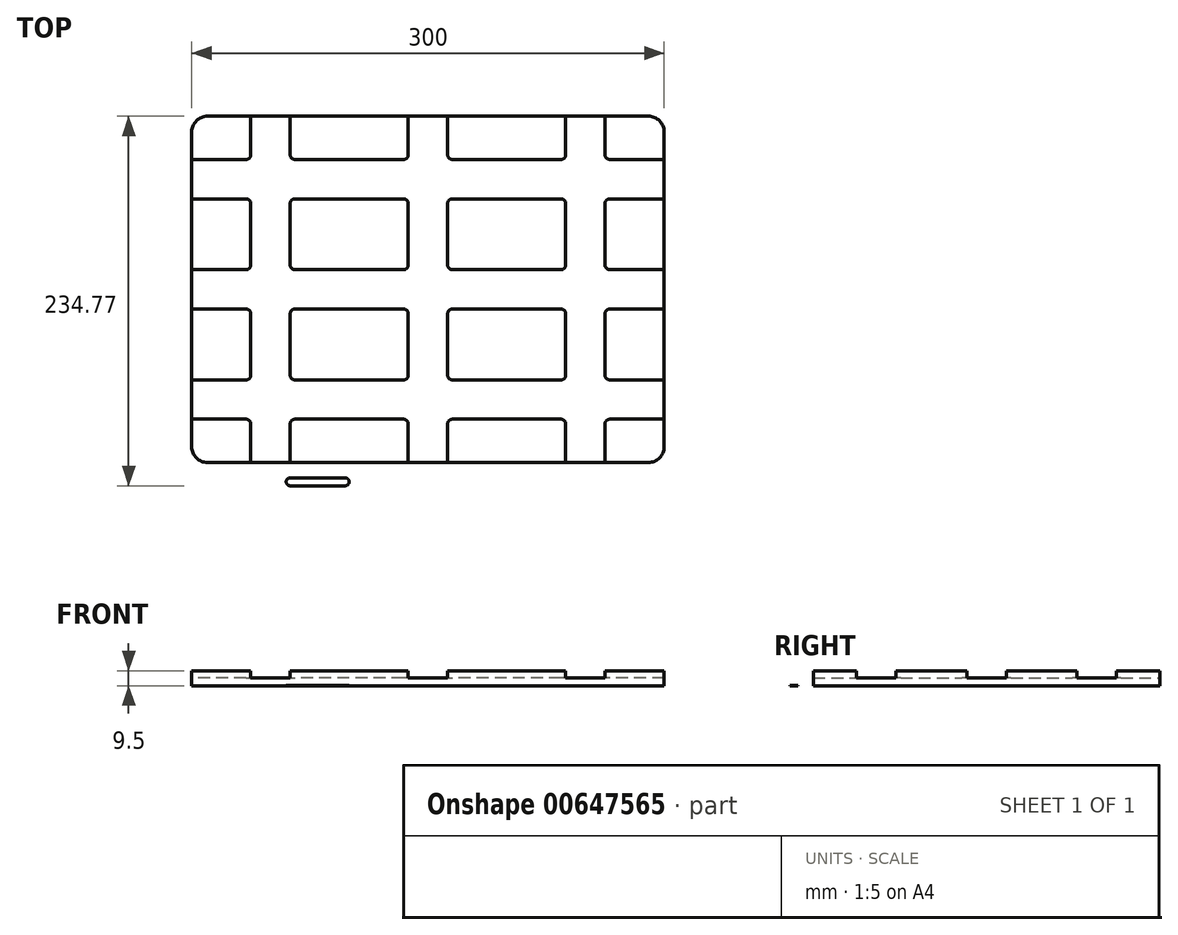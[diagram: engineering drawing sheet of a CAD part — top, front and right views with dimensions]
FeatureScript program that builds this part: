
annotation { "Feature Type Name" : "Feature", "Feature Type Description" : "" }
export const myFeature = defineFeature(function(context is Context, id is Id, definition is map)
    precondition{}
    {
        {
            var Q0;
            Q0=qCreatedBy(makeId("Top.planeOp"),FACE);
            var sketch = newSketch(context, id + "F0", { "sketchPlane" : qUnion([Q0])});
            skLineSegment(sketch, "E0.bottom", {"start": v(140, -110) * mm, "end": v(-140, -110) * mm});
            skLineSegment(sketch, "E0.top", {"start": v(140, 110) * mm, "end": v(-140, 110) * mm});
            skLineSegment(sketch, "E0.left", {"start": v(150, -100) * mm, "end": v(150, 100) * mm});
            skLineSegment(sketch, "E0.right", {"start": v(-150, -100) * mm, "end": v(-150, 100) * mm});
            skPoint(sketch, "E0.middle", {"position": v(0, 0) * mm});
            skLineSegment(sketch, "E1", {"start": v(0, 110) * mm, "end": v(0, -110) * mm, "construction": true});
            skLineSegment(sketch, "E2", {"start": v(-12.5, 124.5) * mm, "end": v(12.5, 124.5) * mm});
            skPoint(sketch, "E3", {"position": v(0, 124.5) * mm});
            skLineSegment(sketch, "E4", {"start": v(-12.5, 110) * mm, "end": v(-12.5, 85.5) * mm});
            skLineSegment(sketch, "E5", {"start": v(12.5, 110) * mm, "end": v(12.5, 85.5) * mm});
            skLineSegment(sketch, "E6", {"start": v(-168.64, 12.5) * mm, "end": v(-168.64, -12.5) * mm});
            skPoint(sketch, "E7", {"position": v(-168.64, 0) * mm});
            skLineSegment(sketch, "E8", {"start": v(-150, 12.5) * mm, "end": v(-115.5, 12.5) * mm});
            skLineSegment(sketch, "E9", {"start": v(-150, -12.5) * mm, "end": v(-115.5, -12.5) * mm});
            skLineSegment(sketch, "E10", {"start": v(-100, 110) * mm, "end": v(-100, -110) * mm, "construction": true});
            skLineSegment(sketch, "E11", {"start": v(100, -110) * mm, "end": v(100, 110) * mm, "construction": true});
            skLineSegment(sketch, "E12", {"start": v(-112.5, 122.6) * mm, "end": v(-87.5, 122.6) * mm});
            skPoint(sketch, "E13", {"position": v(-100, 122.6) * mm});
            skLineSegment(sketch, "E14", {"start": v(87.5, 126.02) * mm, "end": v(112.5, 126.02) * mm});
            skPoint(sketch, "E15", {"position": v(100, 126.02) * mm});
            skLineSegment(sketch, "E16", {"start": v(-112.5, 110) * mm, "end": v(-112.5, 85.5) * mm});
            skLineSegment(sketch, "E17", {"start": v(-87.5, 110) * mm, "end": v(-87.5, 85.5) * mm});
            skLineSegment(sketch, "E18", {"start": v(87.5, 110) * mm, "end": v(87.5, 85.5) * mm});
            skLineSegment(sketch, "E19", {"start": v(112.5, 110) * mm, "end": v(112.5, 85.5) * mm});
            skLineSegment(sketch, "E20", {"start": v(-150, 70) * mm, "end": v(150, 70) * mm, "construction": true});
            skLineSegment(sketch, "E21", {"start": v(150, -70) * mm, "end": v(-150, -70) * mm, "construction": true});
            skLineSegment(sketch, "E22", {"start": v(-168.26, 82.5) * mm, "end": v(-168.26, 57.5) * mm});
            skLineSegment(sketch, "E23", {"start": v(-167.5, -57.5) * mm, "end": v(-167.5, -82.5) * mm});
            skPoint(sketch, "E24", {"position": v(-168.26, 70) * mm});
            skPoint(sketch, "E25", {"position": v(-167.5, -70) * mm});
            skLineSegment(sketch, "E26", {"start": v(-150, 82.5) * mm, "end": v(-115.5, 82.5) * mm});
            skLineSegment(sketch, "E27", {"start": v(-150, 57.5) * mm, "end": v(-115.5, 57.5) * mm});
            skLineSegment(sketch, "E28", {"start": v(-150, -57.5) * mm, "end": v(-115.5, -57.5) * mm});
            skLineSegment(sketch, "E29", {"start": v(-150, -82.5) * mm, "end": v(-115.5, -82.5) * mm});
            skLineSegment(sketch, "E30.trimOffspring", {"start": v(-84.5, 82.5) * mm, "end": v(-15.5, 82.5) * mm});
            skLineSegment(sketch, "E31.trimOffspring", {"start": v(-112.5, 54.5) * mm, "end": v(-112.5, 15.5) * mm});
            skLineSegment(sketch, "E32.trimOffspring", {"start": v(-84.5, 57.5) * mm, "end": v(-15.5, 57.5) * mm});
            skLineSegment(sketch, "E33.trimOffspring", {"start": v(-87.5, 54.5) * mm, "end": v(-87.5, 15.5) * mm});
            skLineSegment(sketch, "E34.trimOffspring", {"start": v(-12.5, 54.5) * mm, "end": v(-12.5, 15.5) * mm});
            skLineSegment(sketch, "E35.trimOffspring", {"start": v(15.5, 82.5) * mm, "end": v(84.5, 82.5) * mm});
            skLineSegment(sketch, "E36.trimOffspring", {"start": v(12.5, 54.5) * mm, "end": v(12.5, 15.5) * mm});
            skLineSegment(sketch, "E37.trimOffspring", {"start": v(15.5, 57.5) * mm, "end": v(84.5, 57.5) * mm});
            skLineSegment(sketch, "E38.trimOffspring", {"start": v(87.5, 54.5) * mm, "end": v(87.5, 15.5) * mm});
            skLineSegment(sketch, "E39.trimOffspring", {"start": v(115.5, 57.5) * mm, "end": v(150, 57.5) * mm});
            skLineSegment(sketch, "E40.trimOffspring", {"start": v(112.5, 54.5) * mm, "end": v(112.5, 15.5) * mm});
            skLineSegment(sketch, "E41.trimOffspring", {"start": v(-84.5, 12.5) * mm, "end": v(-15.5, 12.5) * mm});
            skLineSegment(sketch, "E42.trimOffspring", {"start": v(-84.5, -12.5) * mm, "end": v(-15.5, -12.5) * mm});
            skLineSegment(sketch, "E43.trimOffspring", {"start": v(-112.5, -15.5) * mm, "end": v(-112.5, -54.5) * mm});
            skLineSegment(sketch, "E44.trimOffspring", {"start": v(-87.5, -15.5) * mm, "end": v(-87.5, -54.5) * mm});
            skLineSegment(sketch, "E45.trimOffspring", {"start": v(-12.5, -15.5) * mm, "end": v(-12.5, -54.5) * mm});
            skLineSegment(sketch, "E46.trimOffspring", {"start": v(12.5, -15.5) * mm, "end": v(12.5, -54.5) * mm});
            skLineSegment(sketch, "E47.trimOffspring", {"start": v(87.5, -15.5) * mm, "end": v(87.5, -54.5) * mm});
            skLineSegment(sketch, "E48.trimOffspring", {"start": v(112.5, -15.5) * mm, "end": v(112.5, -54.5) * mm});
            skLineSegment(sketch, "E49.trimOffspring", {"start": v(115.5, 12.5) * mm, "end": v(150, 12.5) * mm});
            skLineSegment(sketch, "E50.trimOffspring", {"start": v(115.5, -12.5) * mm, "end": v(150, -12.5) * mm});
            skLineSegment(sketch, "E51.trimOffspring", {"start": v(-112.5, -85.5) * mm, "end": v(-112.5, -110) * mm});
            skLineSegment(sketch, "E52.trimOffspring", {"start": v(-84.5, -82.5) * mm, "end": v(-15.5, -82.5) * mm});
            skLineSegment(sketch, "E53.trimOffspring", {"start": v(-87.5, -85.5) * mm, "end": v(-87.5, -110) * mm});
            skLineSegment(sketch, "E54.trimOffspring", {"start": v(-84.5, -57.5) * mm, "end": v(-15.5, -57.5) * mm});
            skLineSegment(sketch, "E55.trimOffspring", {"start": v(15.5, -57.5) * mm, "end": v(84.5, -57.5) * mm});
            skLineSegment(sketch, "E56.trimOffspring", {"start": v(-12.5, -85.5) * mm, "end": v(-12.5, -110) * mm});
            skLineSegment(sketch, "E57.trimOffspring", {"start": v(15.5, -82.5) * mm, "end": v(84.5, -82.5) * mm});
            skLineSegment(sketch, "E58.trimOffspring", {"start": v(12.5, -85.5) * mm, "end": v(12.5, -110) * mm});
            skLineSegment(sketch, "E59.trimOffspring", {"start": v(87.5, -85.5) * mm, "end": v(87.5, -110) * mm});
            skLineSegment(sketch, "E60.trimOffspring", {"start": v(115.5, -82.5) * mm, "end": v(150, -82.5) * mm});
            skLineSegment(sketch, "E61.trimOffspring", {"start": v(112.5, -85.5) * mm, "end": v(112.5, -110) * mm});
            skLineSegment(sketch, "E62.trimOffspring", {"start": v(115.5, -57.5) * mm, "end": v(150, -57.5) * mm});
            skLineSegment(sketch, "E63.trimOffspring", {"start": v(115.5, 82.5) * mm, "end": v(150, 82.5) * mm});
            skPoint(sketch, "E64.visualSharp", {"position": v(-150, 110) * mm});
            skArc(sketch, "E64.filletArc", {"start": v(-140, 110) * mm, "mid": v(-147.07, 107.07) * mm, "end": v(-150, 100) * mm});
            skPoint(sketch, "E65.visualSharp", {"position": v(-150, -110) * mm});
            skArc(sketch, "E65.filletArc", {"start": v(-150, -100) * mm, "mid": v(-147.07, -107.07) * mm, "end": v(-140, -110) * mm});
            skPoint(sketch, "E66.visualSharp", {"position": v(150, -110) * mm});
            skArc(sketch, "E66.filletArc", {"start": v(140, -110) * mm, "mid": v(147.07, -107.07) * mm, "end": v(150, -100) * mm});
            skPoint(sketch, "E67.visualSharp", {"position": v(150, 110) * mm});
            skArc(sketch, "E67.filletArc", {"start": v(150, 100) * mm, "mid": v(147.07, 107.07) * mm, "end": v(140, 110) * mm});
            skPoint(sketch, "E68.visualSharp", {"position": v(112.5, -82.5) * mm});
            skArc(sketch, "E68.filletArc", {"start": v(115.5, -82.5) * mm, "mid": v(113.38, -83.38) * mm, "end": v(112.5, -85.5) * mm});
            skPoint(sketch, "E69.visualSharp", {"position": v(87.5, -82.5) * mm});
            skArc(sketch, "E69.filletArc", {"start": v(87.5, -85.5) * mm, "mid": v(86.62, -83.38) * mm, "end": v(84.5, -82.5) * mm});
            skPoint(sketch, "E70.visualSharp", {"position": v(112.5, -57.5) * mm});
            skArc(sketch, "E70.filletArc", {"start": v(112.5, -54.5) * mm, "mid": v(113.38, -56.62) * mm, "end": v(115.5, -57.5) * mm});
            skPoint(sketch, "E71.visualSharp", {"position": v(87.5, -57.5) * mm});
            skArc(sketch, "E71.filletArc", {"start": v(84.5, -57.5) * mm, "mid": v(86.62, -56.62) * mm, "end": v(87.5, -54.5) * mm});
            skPoint(sketch, "E72.visualSharp", {"position": v(12.5, -82.5) * mm});
            skArc(sketch, "E72.filletArc", {"start": v(15.5, -82.5) * mm, "mid": v(13.38, -83.38) * mm, "end": v(12.5, -85.5) * mm});
            skPoint(sketch, "E73.visualSharp", {"position": v(-12.5, -82.5) * mm});
            skArc(sketch, "E73.filletArc", {"start": v(-12.5, -85.5) * mm, "mid": v(-13.38, -83.38) * mm, "end": v(-15.5, -82.5) * mm});
            skPoint(sketch, "E74.visualSharp", {"position": v(-12.5, -57.5) * mm});
            skArc(sketch, "E74.filletArc", {"start": v(-15.5, -57.5) * mm, "mid": v(-13.38, -56.62) * mm, "end": v(-12.5, -54.5) * mm});
            skLineSegment(sketch, "E75.trimOffspring", {"start": v(15.5, 12.5) * mm, "end": v(84.5, 12.5) * mm});
            skPoint(sketch, "E76.visualSharp", {"position": v(12.5, -57.5) * mm});
            skArc(sketch, "E76.filletArc", {"start": v(12.5, -54.5) * mm, "mid": v(13.38, -56.62) * mm, "end": v(15.5, -57.5) * mm});
            skPoint(sketch, "E77.visualSharp", {"position": v(12.5, 12.5) * mm});
            skArc(sketch, "E77.filletArc", {"start": v(12.5, 15.5) * mm, "mid": v(13.38, 13.38) * mm, "end": v(15.5, 12.5) * mm});
            skPoint(sketch, "E78.visualSharp", {"position": v(87.5, 12.5) * mm});
            skArc(sketch, "E78.filletArc", {"start": v(84.5, 12.5) * mm, "mid": v(86.62, 13.38) * mm, "end": v(87.5, 15.5) * mm});
            skPoint(sketch, "E79.visualSharp", {"position": v(112.5, 12.5) * mm});
            skArc(sketch, "E79.filletArc", {"start": v(112.5, 15.5) * mm, "mid": v(113.38, 13.38) * mm, "end": v(115.5, 12.5) * mm});
            skPoint(sketch, "E80.visualSharp", {"position": v(87.5, -12.5) * mm});
            skArc(sketch, "E80.filletArc", {"start": v(87.5, -15.5) * mm, "mid": v(86.62, -13.38) * mm, "end": v(84.5, -12.5) * mm});
            skPoint(sketch, "E81.visualSharp", {"position": v(112.5, -12.5) * mm});
            skArc(sketch, "E81.filletArc", {"start": v(115.5, -12.5) * mm, "mid": v(113.38, -13.38) * mm, "end": v(112.5, -15.5) * mm});
            skPoint(sketch, "E82.visualSharp", {"position": v(-87.5, -57.5) * mm});
            skArc(sketch, "E82.filletArc", {"start": v(-87.5, -54.5) * mm, "mid": v(-86.62, -56.62) * mm, "end": v(-84.5, -57.5) * mm});
            skPoint(sketch, "E83.visualSharp", {"position": v(-87.5, -12.5) * mm});
            skArc(sketch, "E83.filletArc", {"start": v(-84.5, -12.5) * mm, "mid": v(-86.62, -13.38) * mm, "end": v(-87.5, -15.5) * mm});
            skPoint(sketch, "E84.visualSharp", {"position": v(-87.5, 12.5) * mm});
            skArc(sketch, "E84.filletArc", {"start": v(-87.5, 15.5) * mm, "mid": v(-86.62, 13.38) * mm, "end": v(-84.5, 12.5) * mm});
            skPoint(sketch, "E85.visualSharp", {"position": v(-12.5, 12.5) * mm});
            skArc(sketch, "E85.filletArc", {"start": v(-15.5, 12.5) * mm, "mid": v(-13.38, 13.38) * mm, "end": v(-12.5, 15.5) * mm});
            skPoint(sketch, "E86.visualSharp", {"position": v(-12.5, 57.5) * mm});
            skArc(sketch, "E86.filletArc", {"start": v(-12.5, 54.5) * mm, "mid": v(-13.38, 56.62) * mm, "end": v(-15.5, 57.5) * mm});
            skPoint(sketch, "E87.visualSharp", {"position": v(12.5, 57.5) * mm});
            skArc(sketch, "E87.filletArc", {"start": v(15.5, 57.5) * mm, "mid": v(13.38, 56.62) * mm, "end": v(12.5, 54.5) * mm});
            skPoint(sketch, "E88.visualSharp", {"position": v(112.5, 82.5) * mm});
            skArc(sketch, "E88.filletArc", {"start": v(112.5, 85.5) * mm, "mid": v(113.38, 83.38) * mm, "end": v(115.5, 82.5) * mm});
            skPoint(sketch, "E89.visualSharp", {"position": v(87.5, 82.5) * mm});
            skArc(sketch, "E89.filletArc", {"start": v(84.5, 82.5) * mm, "mid": v(86.62, 83.38) * mm, "end": v(87.5, 85.5) * mm});
            skPoint(sketch, "E90.visualSharp", {"position": v(12.5, 82.5) * mm});
            skArc(sketch, "E90.filletArc", {"start": v(12.5, 85.5) * mm, "mid": v(13.38, 83.38) * mm, "end": v(15.5, 82.5) * mm});
            skPoint(sketch, "E91.visualSharp", {"position": v(-12.5, 82.5) * mm});
            skArc(sketch, "E91.filletArc", {"start": v(-15.5, 82.5) * mm, "mid": v(-13.38, 83.38) * mm, "end": v(-12.5, 85.5) * mm});
            skPoint(sketch, "E92.visualSharp", {"position": v(-87.5, 82.5) * mm});
            skArc(sketch, "E92.filletArc", {"start": v(-87.5, 85.5) * mm, "mid": v(-86.62, 83.38) * mm, "end": v(-84.5, 82.5) * mm});
            skPoint(sketch, "E93.visualSharp", {"position": v(-112.5, 82.5) * mm});
            skArc(sketch, "E93.filletArc", {"start": v(-115.5, 82.5) * mm, "mid": v(-113.38, 83.38) * mm, "end": v(-112.5, 85.5) * mm});
            skPoint(sketch, "E94.visualSharp", {"position": v(-112.5, 57.5) * mm});
            skArc(sketch, "E94.filletArc", {"start": v(-112.5, 54.5) * mm, "mid": v(-113.38, 56.62) * mm, "end": v(-115.5, 57.5) * mm});
            skPoint(sketch, "E95.visualSharp", {"position": v(-87.5, 57.5) * mm});
            skArc(sketch, "E95.filletArc", {"start": v(-84.5, 57.5) * mm, "mid": v(-86.62, 56.62) * mm, "end": v(-87.5, 54.5) * mm});
            skPoint(sketch, "E96.visualSharp", {"position": v(-112.5, 12.5) * mm});
            skArc(sketch, "E96.filletArc", {"start": v(-115.5, 12.5) * mm, "mid": v(-113.38, 13.38) * mm, "end": v(-112.5, 15.5) * mm});
            skPoint(sketch, "E97.visualSharp", {"position": v(-112.5, -12.5) * mm});
            skArc(sketch, "E97.filletArc", {"start": v(-112.5, -15.5) * mm, "mid": v(-113.38, -13.38) * mm, "end": v(-115.5, -12.5) * mm});
            skPoint(sketch, "E98.visualSharp", {"position": v(-112.5, -57.5) * mm});
            skArc(sketch, "E98.filletArc", {"start": v(-115.5, -57.5) * mm, "mid": v(-113.38, -56.62) * mm, "end": v(-112.5, -54.5) * mm});
            skPoint(sketch, "E99.visualSharp", {"position": v(-112.5, -82.5) * mm});
            skArc(sketch, "E99.filletArc", {"start": v(-112.5, -85.5) * mm, "mid": v(-113.38, -83.38) * mm, "end": v(-115.5, -82.5) * mm});
            skPoint(sketch, "E100.visualSharp", {"position": v(-87.5, -82.5) * mm});
            skArc(sketch, "E100.filletArc", {"start": v(-84.5, -82.5) * mm, "mid": v(-86.62, -83.38) * mm, "end": v(-87.5, -85.5) * mm});
            skPoint(sketch, "E101.visualSharp", {"position": v(112.5, 57.5) * mm});
            skArc(sketch, "E101.filletArc", {"start": v(115.5, 57.5) * mm, "mid": v(113.38, 56.62) * mm, "end": v(112.5, 54.5) * mm});
            skPoint(sketch, "E102.visualSharp", {"position": v(87.5, 57.5) * mm});
            skArc(sketch, "E102.filletArc", {"start": v(87.5, 54.5) * mm, "mid": v(86.62, 56.62) * mm, "end": v(84.5, 57.5) * mm});
            skLineSegment(sketch, "E103.trimOffspring", {"start": v(15.5, -12.5) * mm, "end": v(84.5, -12.5) * mm});
            skPoint(sketch, "E104.visualSharp", {"position": v(12.5, -12.5) * mm});
            skArc(sketch, "E104.filletArc", {"start": v(15.5, -12.5) * mm, "mid": v(13.38, -13.38) * mm, "end": v(12.5, -15.5) * mm});
            skPoint(sketch, "E105.visualSharp", {"position": v(-12.5, -12.5) * mm});
            skArc(sketch, "E105.filletArc", {"start": v(-12.5, -15.5) * mm, "mid": v(-13.38, -13.38) * mm, "end": v(-15.5, -12.5) * mm});
            skLineSegment(sketch, "E106.bottom", {"start": v(-87.5, -119.77) * mm, "end": v(-52.5, -119.77) * mm});
            skLineSegment(sketch, "E106.top", {"start": v(-87.5, -124.77) * mm, "end": v(-52.5, -124.77) * mm});
            skLineSegment(sketch, "E106.left", {"start": v(-87.5, -119.77) * mm, "end": v(-87.5, -124.77) * mm});
            skLineSegment(sketch, "E106.right", {"start": v(-52.5, -119.77) * mm, "end": v(-52.5, -124.77) * mm});
            skArc(sketch, "E107", {"start": v(-87.5, -119.77) * mm, "mid": v(-90, -122.27) * mm, "end": v(-87.5, -124.77) * mm});
            skArc(sketch, "E108", {"start": v(-52.5, -124.77) * mm, "mid": v(-50, -122.27) * mm, "end": v(-52.5, -119.77) * mm});
            skSolve(sketch);
        }
        {
            var Q0;
            {var subQ0=sQuery(id+"F0.wireOp",EDGE,"E16");Q0=makeQuery(id+"F0.imprint","IMPRINT",FACE,{"disambiguationData":[TD([[makeQuery(id+"F0.imprint","IMPRINT",EDGE,{"derivedFrom":subQ0}),-1.0]])]});}
            var Q1;
            {var subQ21=sQuery(id+"F0.wireOp",EDGE,"E4");Q1=makeQuery(id+"F0.imprint","IMPRINT",FACE,{"disambiguationData":[TD([[makeQuery(id+"F0.imprint","IMPRINT",EDGE,{"derivedFrom":subQ21}),1.0]])]});}
            var Q2;
            {var subQ0=sQuery(id+"F0.wireOp",EDGE,"E4");Q2=makeQuery(id+"F0.imprint","IMPRINT",FACE,{"disambiguationData":[TD([[makeQuery(id+"F0.imprint","IMPRINT",EDGE,{"derivedFrom":subQ0}),-1.0]])]});}
            var Q3;
            {var subQ2=sQuery(id+"F0.wireOp",EDGE,"E5");Q3=makeQuery(id+"F0.imprint","IMPRINT",FACE,{"disambiguationData":[TD([[makeQuery(id+"F0.imprint","IMPRINT",EDGE,{"derivedFrom":subQ2}),1.0]])]});}
            var Q4;
            {var subQ3=sQuery(id+"F0.wireOp",EDGE,"E19");Q4=makeQuery(id+"F0.imprint","IMPRINT",FACE,{"disambiguationData":[TD([[makeQuery(id+"F0.imprint","IMPRINT",EDGE,{"derivedFrom":subQ3}),1.0]])]});}
            var Q5;
            {var subQ0=sQuery(id+"F0.wireOp",EDGE,"E39.trimOffspring");Q5=makeQuery(id+"F0.imprint","IMPRINT",FACE,{"disambiguationData":[TD([[makeQuery(id+"F0.imprint","IMPRINT",EDGE,{"derivedFrom":subQ0}),-1.0]])]});}
            var Q6;
            {var subQ0=sQuery(id+"F0.wireOp",EDGE,"E36.trimOffspring");Q6=makeQuery(id+"F0.imprint","IMPRINT",FACE,{"disambiguationData":[TD([[makeQuery(id+"F0.imprint","IMPRINT",EDGE,{"derivedFrom":subQ0}),1.0]])]});}
            var Q7;
            Q7=makeQuery(id+"F0.imprint","IMPRINT",FACE,{"disambiguationData":[TD([[makeQuery(id+"F0.imprint","IMPRINT",EDGE,{"derivedFrom":sQuery(id+"F0.wireOp",EDGE,"E32.trimOffspring")}),-1.0]])]});
            var Q8;
            {var subQ0=sQuery(id+"F0.wireOp",EDGE,"E8");Q8=makeQuery(id+"F0.imprint","IMPRINT",FACE,{"disambiguationData":[TD([[makeQuery(id+"F0.imprint","IMPRINT",EDGE,{"derivedFrom":subQ0}),1.0]])]});}
            var Q9;
            {var subQ0=sQuery(id+"F0.wireOp",EDGE,"E9");Q9=makeQuery(id+"F0.imprint","IMPRINT",FACE,{"disambiguationData":[TD([[makeQuery(id+"F0.imprint","IMPRINT",EDGE,{"derivedFrom":subQ0}),-1.0]])]});}
            var Q10;
            {var subQ0=sQuery(id+"F0.wireOp",EDGE,"E44.trimOffspring");Q10=makeQuery(id+"F0.imprint","IMPRINT",FACE,{"disambiguationData":[TD([[makeQuery(id+"F0.imprint","IMPRINT",EDGE,{"derivedFrom":subQ0}),1.0]])]});}
            var Q11;
            {var subQ0=sQuery(id+"F0.wireOp",EDGE,"E46.trimOffspring");Q11=makeQuery(id+"F0.imprint","IMPRINT",FACE,{"disambiguationData":[TD([[makeQuery(id+"F0.imprint","IMPRINT",EDGE,{"derivedFrom":subQ0}),1.0]])]});}
            var Q12;
            Q12=makeQuery(id+"F0.imprint","IMPRINT",FACE,{"disambiguationData":[TD([[makeQuery(id+"F0.imprint","IMPRINT",EDGE,{"derivedFrom":sQuery(id+"F0.wireOp",EDGE,"E48.trimOffspring")}),1.0]])]});
            var Q13;
            {var subQ1=sQuery(id+"F0.wireOp",EDGE,"E60.trimOffspring");Q13=makeQuery(id+"F0.imprint","IMPRINT",FACE,{"disambiguationData":[TD([[makeQuery(id+"F0.imprint","IMPRINT",EDGE,{"derivedFrom":subQ1}),-1.0]])]});}
            var Q14;
            Q14=makeQuery(id+"F0.imprint","IMPRINT",FACE,{"disambiguationData":[TD([[makeQuery(id+"F0.imprint","IMPRINT",EDGE,{"derivedFrom":sQuery(id+"F0.wireOp",EDGE,"E57.trimOffspring")}),-1.0]])]});
            var Q15;
            Q15=makeQuery(id+"F0.imprint","IMPRINT",FACE,{"disambiguationData":[TD([[makeQuery(id+"F0.imprint","IMPRINT",EDGE,{"derivedFrom":sQuery(id+"F0.wireOp",EDGE,"E52.trimOffspring")}),-1.0]])]});
            var Q16;
            {var subQ0=sQuery(id+"F0.wireOp",EDGE,"E29");Q16=makeQuery(id+"F0.imprint","IMPRINT",FACE,{"disambiguationData":[TD([[makeQuery(id+"F0.imprint","IMPRINT",EDGE,{"derivedFrom":subQ0}),-1.0]])]});}
            extrude(context, id + "F1", {"entities" : qUnion([Q0, Q1, Q2, Q3, Q4, Q5, Q6, Q7, Q8, Q9, Q10, Q11, Q12, Q13, Q14, Q15, Q16]), "depth" : 5 * mm, "offsetDistance" : 25 * mm});
        }
        {
            var Q0;
            {var subQ0=sQuery(id+"F0.wireOp",EDGE,"E8");Q0=makeQuery(id+"F0.imprint","IMPRINT",FACE,{"disambiguationData":[TD([[makeQuery(id+"F0.imprint","IMPRINT",EDGE,{"derivedFrom":subQ0}),1.0]])]});}
            var Q1;
            {var subQ0=sQuery(id+"F0.wireOp",EDGE,"E16");Q1=makeQuery(id+"F0.imprint","IMPRINT",FACE,{"disambiguationData":[TD([[makeQuery(id+"F0.imprint","IMPRINT",EDGE,{"derivedFrom":subQ0}),-1.0]])]});}
            var Q2;
            {var subQ0=sQuery(id+"F0.wireOp",EDGE,"E4");Q2=makeQuery(id+"F0.imprint","IMPRINT",FACE,{"disambiguationData":[TD([[makeQuery(id+"F0.imprint","IMPRINT",EDGE,{"derivedFrom":subQ0}),-1.0]])]});}
            var Q3;
            Q3=makeQuery(id+"F0.imprint","IMPRINT",FACE,{"disambiguationData":[TD([[makeQuery(id+"F0.imprint","IMPRINT",EDGE,{"derivedFrom":sQuery(id+"F0.wireOp",EDGE,"E32.trimOffspring")}),-1.0]])]});
            var Q4;
            {var subQ0=sQuery(id+"F0.wireOp",EDGE,"E44.trimOffspring");Q4=makeQuery(id+"F0.imprint","IMPRINT",FACE,{"disambiguationData":[TD([[makeQuery(id+"F0.imprint","IMPRINT",EDGE,{"derivedFrom":subQ0}),1.0]])]});}
            var Q5;
            {var subQ0=sQuery(id+"F0.wireOp",EDGE,"E9");Q5=makeQuery(id+"F0.imprint","IMPRINT",FACE,{"disambiguationData":[TD([[makeQuery(id+"F0.imprint","IMPRINT",EDGE,{"derivedFrom":subQ0}),-1.0]])]});}
            var Q6;
            {var subQ0=sQuery(id+"F0.wireOp",EDGE,"E29");Q6=makeQuery(id+"F0.imprint","IMPRINT",FACE,{"disambiguationData":[TD([[makeQuery(id+"F0.imprint","IMPRINT",EDGE,{"derivedFrom":subQ0}),-1.0]])]});}
            var Q7;
            Q7=makeQuery(id+"F0.imprint","IMPRINT",FACE,{"disambiguationData":[TD([[makeQuery(id+"F0.imprint","IMPRINT",EDGE,{"derivedFrom":sQuery(id+"F0.wireOp",EDGE,"E52.trimOffspring")}),-1.0]])]});
            var Q8;
            Q8=makeQuery(id+"F0.imprint","IMPRINT",FACE,{"disambiguationData":[TD([[makeQuery(id+"F0.imprint","IMPRINT",EDGE,{"derivedFrom":sQuery(id+"F0.wireOp",EDGE,"E57.trimOffspring")}),-1.0]])]});
            var Q9;
            {var subQ0=sQuery(id+"F0.wireOp",EDGE,"E46.trimOffspring");Q9=makeQuery(id+"F0.imprint","IMPRINT",FACE,{"disambiguationData":[TD([[makeQuery(id+"F0.imprint","IMPRINT",EDGE,{"derivedFrom":subQ0}),1.0]])]});}
            var Q10;
            {var subQ0=sQuery(id+"F0.wireOp",EDGE,"E36.trimOffspring");Q10=makeQuery(id+"F0.imprint","IMPRINT",FACE,{"disambiguationData":[TD([[makeQuery(id+"F0.imprint","IMPRINT",EDGE,{"derivedFrom":subQ0}),1.0]])]});}
            var Q11;
            {var subQ2=sQuery(id+"F0.wireOp",EDGE,"E5");Q11=makeQuery(id+"F0.imprint","IMPRINT",FACE,{"disambiguationData":[TD([[makeQuery(id+"F0.imprint","IMPRINT",EDGE,{"derivedFrom":subQ2}),1.0]])]});}
            var Q12;
            {var subQ3=sQuery(id+"F0.wireOp",EDGE,"E19");Q12=makeQuery(id+"F0.imprint","IMPRINT",FACE,{"disambiguationData":[TD([[makeQuery(id+"F0.imprint","IMPRINT",EDGE,{"derivedFrom":subQ3}),1.0]])]});}
            var Q13;
            {var subQ0=sQuery(id+"F0.wireOp",EDGE,"E39.trimOffspring");Q13=makeQuery(id+"F0.imprint","IMPRINT",FACE,{"disambiguationData":[TD([[makeQuery(id+"F0.imprint","IMPRINT",EDGE,{"derivedFrom":subQ0}),-1.0]])]});}
            var Q14;
            Q14=makeQuery(id+"F0.imprint","IMPRINT",FACE,{"disambiguationData":[TD([[makeQuery(id+"F0.imprint","IMPRINT",EDGE,{"derivedFrom":sQuery(id+"F0.wireOp",EDGE,"E48.trimOffspring")}),1.0]])]});
            var Q15;
            {var subQ1=sQuery(id+"F0.wireOp",EDGE,"E60.trimOffspring");Q15=makeQuery(id+"F0.imprint","IMPRINT",FACE,{"disambiguationData":[TD([[makeQuery(id+"F0.imprint","IMPRINT",EDGE,{"derivedFrom":subQ1}),-1.0]])]});}
            extrude(context, id + "F2", {"entities" : qUnion([Q0, Q1, Q2, Q3, Q4, Q5, Q6, Q7, Q8, Q9, Q10, Q11, Q12, Q13, Q14, Q15]), "operationType" : NewBodyOperationType.ADD, "depth" : 9.5 * mm, "offsetDistance" : 25 * mm});
        }
        {
            var Q0;
            Q0=makeQuery(id+"F0.imprint","IMPRINT",FACE,{"disambiguationData":[TD([[makeQuery(id+"F0.imprint","IMPRINT",EDGE,{"derivedFrom":sQuery(id+"F0.wireOp",EDGE,"E106.bottom")}),-1.0]])]});
            var Q1;
            Q1=makeQuery(id+"F0.imprint","IMPRINT",FACE,{"disambiguationData":[TD([[makeQuery(id+"F0.imprint","IMPRINT",EDGE,{"derivedFrom":sQuery(id+"F0.wireOp",EDGE,"E106.right")}),1.0]])]});
            var Q2;
            Q2=makeQuery(id+"F0.imprint","IMPRINT",FACE,{"disambiguationData":[TD([[makeQuery(id+"F0.imprint","IMPRINT",EDGE,{"derivedFrom":sQuery(id+"F0.wireOp",EDGE,"E106.left")}),-1.0]])]});
            extrude(context, id + "F3", {"entities" : qUnion([Q0, Q1, Q2]), "depth" : .3 * mm, "offsetDistance" : 25 * mm});
        }
    });
